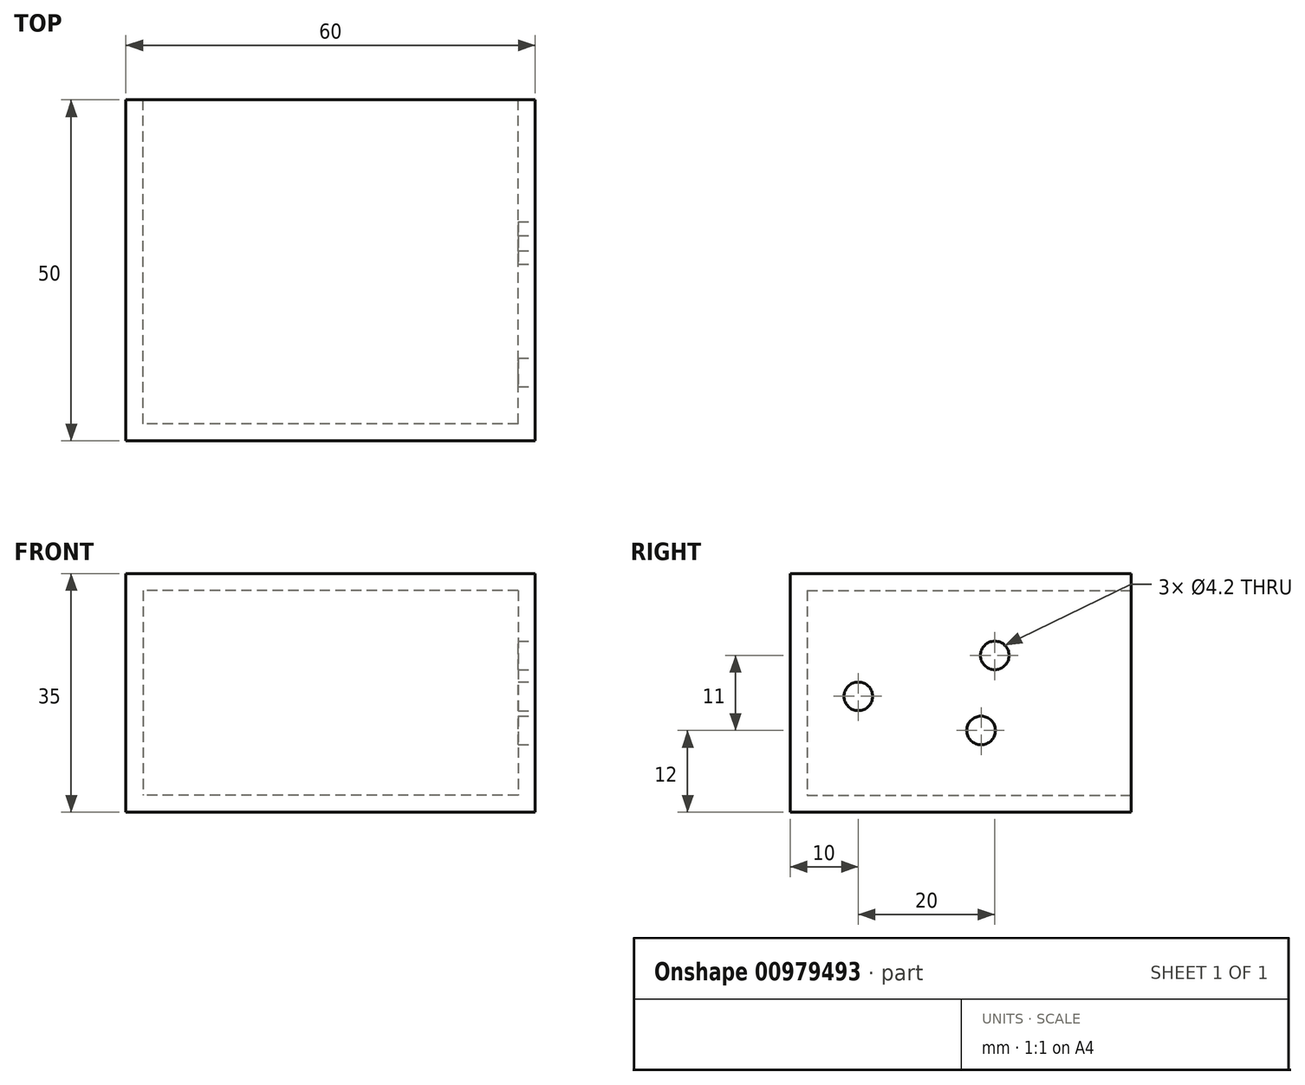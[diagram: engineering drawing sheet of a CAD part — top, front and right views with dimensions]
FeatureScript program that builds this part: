
annotation { "Feature Type Name" : "Feature", "Feature Type Description" : "" }
export const myFeature = defineFeature(function(context is Context, id is Id, definition is map)
    precondition{}
    {
        {
            var Q0;
            Q0=qCreatedBy(makeId("Front.planeOp"),FACE);
            var sketch = newSketch(context, id + "F0", { "sketchPlane" : qUnion([Q0])});
            skLineSegment(sketch, "E0.bottom", {"start": v(30, 17.5) * mm, "end": v(-30, 17.5) * mm});
            skLineSegment(sketch, "E0.top", {"start": v(30, -17.5) * mm, "end": v(-30, -17.5) * mm});
            skLineSegment(sketch, "E0.left", {"start": v(30, 17.5) * mm, "end": v(30, -17.5) * mm});
            skLineSegment(sketch, "E0.right", {"start": v(-30, 17.5) * mm, "end": v(-30, -17.5) * mm});
            skPoint(sketch, "E0.middle", {"position": v(0, 0) * mm});
            skSolve(sketch);
        }
        {
            var Q0;
            Q0 = qSketchRegion(id + "F0", true);
            extrude(context, id + "F1", {"entities" : qUnion([Q0]), "depth" : 50 * mm, "offsetDistance" : 25 * mm});
        }
        {
            var Q0;
            Q0=makeQuery(id+"F1.opExtrude","CAP_FACE",FACE,{"disambiguationData":[OSD([sQuery(id+"F0.wireOp",EDGE,"E0.bottom"),sQuery(id+"F0.wireOp",EDGE,"E0.top"),sQuery(id+"F0.wireOp",EDGE,"E0.left"),sQuery(id+"F0.wireOp",EDGE,"E0.right")])],"isStart":true});
            shell(context, id + "F2", {"entities" : qUnion([Q0]), "thickness" : 2.5 * mm});
        }
        {
            var Q0;
            Q0=makeQuery(id+"F1.opExtrude","SWEPT_FACE",FACE,{"disambiguationData":[OSD([sQuery(id+"F0.wireOp",EDGE,"E0.left")])]});
            var sketch = newSketch(context, id + "F3", { "sketchPlane" : qUnion([Q0])});
            skPoint(sketch, "E1", {"position": v(-40, -0.5) * mm});
            skPoint(sketch, "E2", {"position": v(-22, -5.5) * mm});
            skPoint(sketch, "E3", {"position": v(-20, 5.5) * mm});
            skSolve(sketch);
        }
        {
            var Q0;
            Q0=sQuery(id+"F3.wireOp",VERTEX,"E1");
            var Q1;
            Q1=sQuery(id+"F3.wireOp",VERTEX,"E3");
            var Q2;
            Q2=sQuery(id+"F3.wireOp",VERTEX,"E2");
            var Q3;
            Q3=makeQuery(id+"F1.opExtrude","SWEPT_BODY",BODY,{"disambiguationData":[OSD([sQuery(id+"F0.wireOp",EDGE,"E0.bottom"),sQuery(id+"F0.wireOp",EDGE,"E0.top"),sQuery(id+"F0.wireOp",EDGE,"E0.left"),sQuery(id+"F0.wireOp",EDGE,"E0.right")])]});
            hole(context, id + "F4", {"style" : HoleStyle.SIMPLE, "endStyle" : HoleEndStyle.BLIND, "standardTappedOrClearance" : lookupTablePath({ "standard" : "ISO", "engagement" : "75%", "pitch" : "0.8 mm", "size" : "M5", "type" : "Tapped" }), "standardBlindInLast" : lookupTablePath({ "standard" : "ISO", "fit" : "Normal", "engagement" : "75%", "pitch" : "0.8 mm", "size" : "M5", "type" : "Clearance & tapped" }), "holeDiameter" : 4.2 * mm, "majorDiameter" : 5 * mm, "showTappedDepth" : true, "holeDepth" : 14.4 * mm, "isTappedThrough" : true, "tappedDepth" : 12 * mm, "tapClearance" : 3, "startFromSketch" : true, "locations" : qUnion([Q0, Q1, Q2]), "scope" : qUnion([Q3])});
        }
    });
